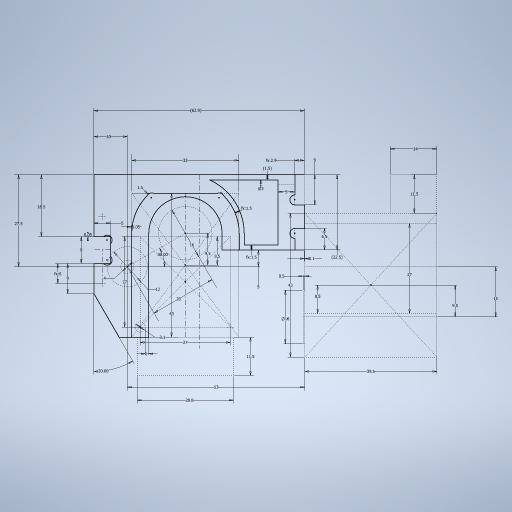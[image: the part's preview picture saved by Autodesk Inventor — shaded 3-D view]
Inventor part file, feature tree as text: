
AUTODESK INVENTOR PART (.ipt)
format: ipt  version: 2024.2 (Build 282272000, 272)  size: 355,840 bytes
history: native  units: mm
features: sketch x1
ambient origin geometry x8: Origin, YZ Plane, XZ Plane, XY Plane, X Axis, Y Axis, Z Axis, Center Point
feature tree (1):
  sketch  "Sketch1"  dims[d0=20.0mm d1=30.0deg d2=32.0mm d3=43.0mm d4=27.0mm d5=27.0mm d6=16.0mm d7=8.5mm d8=9.5mm d9=28.8mm d10=11.5mm d11=39.5mm d12=43.0mm d13=16.0mm d14=9.5mm d15=15.0mm d16=0.5mm d17=14.0mm d18=11.5mm d20=12.0mm d21=4.0mm d22=0.05mm d23=1.5mm d24=5.0mm d26=27.0mm d27=8.5mm d29=30.0deg d32=27.5mm d33=62.9mm d39=8.0mm d40=0.05mm d42=9.0mm d46=6.0mm d65=2.5mm d71=6.0mm d103=53.0mm d104=10.0mm d113=3.1mm d114=1.0mm d115=5.0mm d117=2.9mm d119=22.5mm d121=9.0mm d122=6.5mm d123=0.1mm d124=18.5mm d125=5.0mm d126=3.0mm d127=1.5mm d128=1.5mm d129=1.5mm]
